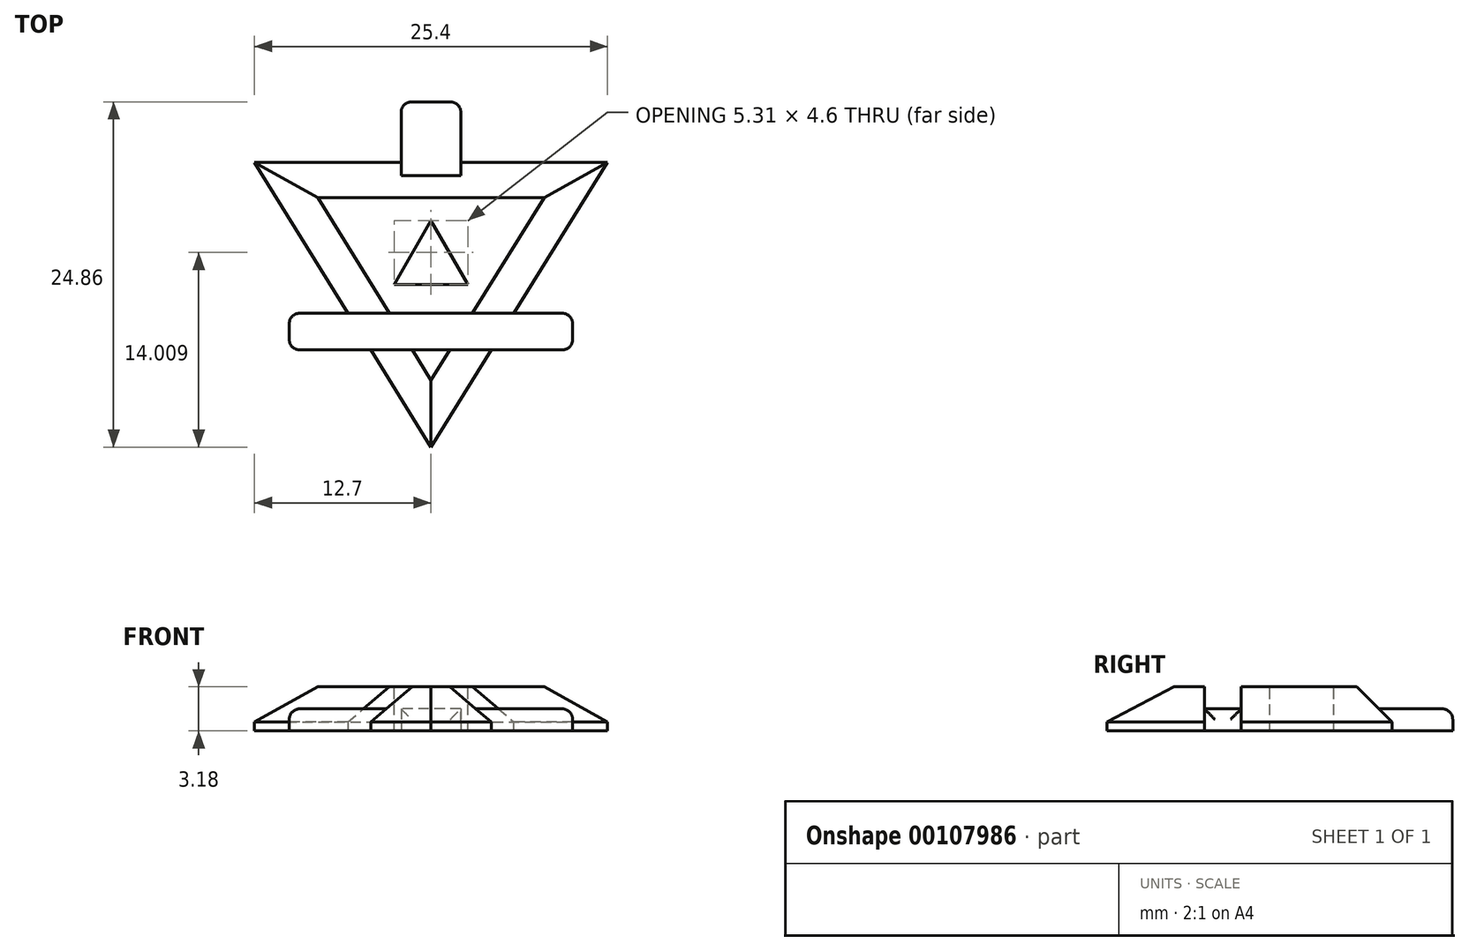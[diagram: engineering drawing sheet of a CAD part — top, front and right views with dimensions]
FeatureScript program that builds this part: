
annotation { "Feature Type Name" : "Feature", "Feature Type Description" : "" }
export const myFeature = defineFeature(function(context is Context, id is Id, definition is map)
    precondition{}
    {
        {
            var Q0;
            Q0=qCreatedBy(makeId("Top.planeOp"),FACE);
            var sketch = newSketch(context, id + "F0", { "sketchPlane" : qUnion([Q0])});
            skLineSegment(sketch, "E0.bottom", {"start": v(-12.7, 12.7) * mm, "end": v(12.7, 12.7) * mm});
            skLineSegment(sketch, "E0.top", {"start": v(-12.7, -12.7) * mm, "end": v(12.7, -12.7) * mm});
            skLineSegment(sketch, "E0.left", {"start": v(-12.7, 12.7) * mm, "end": v(-12.7, -12.7) * mm});
            skLineSegment(sketch, "E0.right", {"start": v(12.7, 12.7) * mm, "end": v(12.7, -12.7) * mm});
            skPoint(sketch, "E0.middle", {"position": v(0, 0) * mm});
            skLineSegment(sketch, "E1", {"start": v(0, -12.7) * mm, "end": v(-12.7, 7.8) * mm});
            skLineSegment(sketch, "E2", {"start": v(-12.7, 7.8) * mm, "end": v(12.7, 7.8) * mm});
            skLineSegment(sketch, "E3", {"start": v(12.7, 7.8) * mm, "end": v(0, -12.7) * mm});
            skSolve(sketch);
        }
        {
            var Q0;
            Q0=makeQuery(id+"F0.imprint","IMPRINT",FACE,{"disambiguationData":[TD([[makeQuery(id+"F0.imprint","IMPRINT",EDGE,{"derivedFrom":sQuery(id+"F0.wireOp",EDGE,"E1")}),-1.0]])]});
            extrude(context, id + "F1", {"entities" : qUnion([Q0]), "depth" : 3.17 * mm});
        }
        {
            var Q0;
            Q0=qCreatedBy(makeId("Top.planeOp"),FACE);
            var sketch = newSketch(context, id + "F2", { "sketchPlane" : qUnion([Q0])});
            skLineSegment(sketch, "E4.bottom", {"start": v(-10.2, -3.06) * mm, "end": v(10.2, -3.06) * mm});
            skLineSegment(sketch, "E4.top", {"start": v(-10.2, -5.7) * mm, "end": v(10.2, -5.7) * mm});
            skLineSegment(sketch, "E4.left", {"start": v(-10.2, -3.06) * mm, "end": v(-10.2, -5.7) * mm});
            skLineSegment(sketch, "E4.right", {"start": v(10.2, -3.06) * mm, "end": v(10.2, -5.7) * mm});
            skPoint(sketch, "E4.middle", {"position": v(0, -4.38) * mm});
            skLineSegment(sketch, "E5.bottom", {"start": v(2.15, 12.16) * mm, "end": v(-2.15, 12.16) * mm});
            skLineSegment(sketch, "E5.top", {"start": v(2.15, -1.67) * mm, "end": v(-2.15, -1.67) * mm});
            skLineSegment(sketch, "E5.left", {"start": v(2.15, 12.16) * mm, "end": v(2.15, -1.67) * mm});
            skLineSegment(sketch, "E5.right", {"start": v(-2.15, 12.16) * mm, "end": v(-2.15, -1.67) * mm});
            skPoint(sketch, "E5.middle", {"position": v(0, 5.25) * mm});
            skSolve(sketch);
        }
        {
            var Q0;
            Q0 = qSketchRegion(id + "F2", true);
            extrude(context, id + "F3", {"entities" : qUnion([Q0]), "operationType" : NewBodyOperationType.ADD, "depth" : 1.59 * mm});
        }
        {
            var Q0;
            {var subQ0=sQuery(id+"F2.wireOp",EDGE,"E4.right");var subQ1=sQuery(id+"F2.wireOp",EDGE,"E4.bottom");var subQ2=sQuery(id+"F2.wireOp",EDGE,"E4.top");Q0=makeQuery(id+"F3.boolean.opBoolean","SPLIT",FACE,{"disambiguationData":[TD([makeQuery(id+"F1.opExtrude","SWEPT_FACE",FACE,{"disambiguationData":[OSD([sQuery(id+"F0.wireOp",EDGE,"E3")])]})])],"derivedFrom":makeQuery(id+"F3.opExtrude","CAP_FACE",FACE,{"disambiguationData":[OSD([subQ1,subQ2,sQuery(id+"F2.wireOp",EDGE,"E4.left"),subQ0])],"isStart":false})});}
            var sketch = newSketch(context, id + "F4", { "sketchPlane" : qUnion([Q0])});
            skLineSegment(sketch, "E6.bottom", {"start": v(5.97, -3.06) * mm, "end": v(-8.4, -3.06) * mm});
            skLineSegment(sketch, "E6.top", {"start": v(5.97, -5.7) * mm, "end": v(-8.4, -5.7) * mm});
            skLineSegment(sketch, "E6.left", {"start": v(5.97, -3.06) * mm, "end": v(5.97, -5.7) * mm});
            skLineSegment(sketch, "E6.right", {"start": v(-8.4, -3.06) * mm, "end": v(-8.4, -5.7) * mm});
            skSolve(sketch);
        }
        {
            var Q0;
            Q0 = qSketchRegion(id + "F4", true);
            extrude(context, id + "F5", {"entities" : qUnion([Q0]), "operationType" : NewBodyOperationType.REMOVE, "depth" : 25.4 * mm});
        }
        {
            var Q0;
            {var subQ0=sQuery(id+"F0.wireOp",EDGE,"E1");var subQ1=sQuery(id+"F0.wireOp",EDGE,"E2");Q0=makeQuery(id+"F5.boolean.opBoolean","SPLIT",EDGE,{"disambiguationData":[TD([makeQuery(id+"F1.opExtrude","SWEPT_FACE",FACE,{"disambiguationData":[OSD([subQ1])]})])],"derivedFrom":makeQuery(id+"F1.opExtrude","CAP_EDGE",EDGE,{"disambiguationData":[OSD([subQ0])],"isStart":false})});}
            var Q1;
            Q1=makeQuery(id+"F1.opExtrude","CAP_EDGE",EDGE,{"disambiguationData":[OSD([sQuery(id+"F0.wireOp",EDGE,"E2")])],"isStart":false});
            var Q2;
            {var subQ0=sQuery(id+"F0.wireOp",EDGE,"E3");var subQ1=sQuery(id+"F0.wireOp",EDGE,"E2");Q2=makeQuery(id+"F5.boolean.opBoolean","SPLIT",EDGE,{"disambiguationData":[TD([makeQuery(id+"F1.opExtrude","SWEPT_FACE",FACE,{"disambiguationData":[OSD([subQ1])]})])],"derivedFrom":makeQuery(id+"F1.opExtrude","CAP_EDGE",EDGE,{"disambiguationData":[OSD([subQ0])],"isStart":false})});}
            var Q3;
            {var subQ0=sQuery(id+"F0.wireOp",EDGE,"E1");var subQ1=sQuery(id+"F0.wireOp",EDGE,"E3");Q3=makeQuery(id+"F5.boolean.opBoolean","SPLIT",EDGE,{"disambiguationData":[TD([makeQuery(id+"F1.opExtrude","SWEPT_FACE",FACE,{"disambiguationData":[OSD([subQ0])]})])],"derivedFrom":makeQuery(id+"F1.opExtrude","CAP_EDGE",EDGE,{"disambiguationData":[OSD([subQ1])],"isStart":false})});}
            var Q4;
            {var subQ0=sQuery(id+"F0.wireOp",EDGE,"E1");var subQ1=sQuery(id+"F0.wireOp",EDGE,"E3");Q4=makeQuery(id+"F5.boolean.opBoolean","SPLIT",EDGE,{"disambiguationData":[TD([makeQuery(id+"F1.opExtrude","SWEPT_FACE",FACE,{"disambiguationData":[OSD([subQ1])]})])],"derivedFrom":makeQuery(id+"F1.opExtrude","CAP_EDGE",EDGE,{"disambiguationData":[OSD([subQ0])],"isStart":false})});}
            chamfer(context, id + "F6", {"entities" : qUnion([Q0, Q1, Q2, Q3, Q4]), "width" : 2.54 * mm, "tangentPropagation" : true});
        }
        {
            var Q0;
            Q0=makeQuery(id+"F3.opExtrude","SWEPT_EDGE",EDGE,{"disambiguationData":[OSD([sQuery(id+"F2.wireOp",EDGE,"E5.bottom"),sQuery(id+"F2.wireOp",EDGE,"E5.right")])]});
            var Q1;
            Q1=makeQuery(id+"F3.opExtrude","CAP_EDGE",EDGE,{"disambiguationData":[OSD([sQuery(id+"F2.wireOp",EDGE,"E5.bottom")])],"isStart":false});
            var Q2;
            Q2=makeQuery(id+"F3.opExtrude","SWEPT_EDGE",EDGE,{"disambiguationData":[OSD([sQuery(id+"F2.wireOp",EDGE,"E5.bottom"),sQuery(id+"F2.wireOp",EDGE,"E5.left")])]});
            var Q3;
            Q3=makeQuery(id+"F3.opExtrude","CAP_EDGE",EDGE,{"disambiguationData":[OSD([sQuery(id+"F2.wireOp",EDGE,"E4.left")])],"isStart":false});
            var Q4;
            Q4=makeQuery(id+"F3.opExtrude","SWEPT_EDGE",EDGE,{"disambiguationData":[OSD([sQuery(id+"F2.wireOp",EDGE,"E4.top"),sQuery(id+"F2.wireOp",EDGE,"E4.left")])]});
            var Q5;
            Q5=makeQuery(id+"F3.opExtrude","SWEPT_EDGE",EDGE,{"disambiguationData":[OSD([sQuery(id+"F2.wireOp",EDGE,"E4.bottom"),sQuery(id+"F2.wireOp",EDGE,"E4.left")])]});
            var Q6;
            Q6=makeQuery(id+"F3.opExtrude","SWEPT_EDGE",EDGE,{"disambiguationData":[OSD([sQuery(id+"F2.wireOp",EDGE,"E4.bottom"),sQuery(id+"F2.wireOp",EDGE,"E4.right")])]});
            var Q7;
            Q7=makeQuery(id+"F3.opExtrude","SWEPT_EDGE",EDGE,{"disambiguationData":[OSD([sQuery(id+"F2.wireOp",EDGE,"E4.top"),sQuery(id+"F2.wireOp",EDGE,"E4.right")])]});
            var Q8;
            Q8=makeQuery(id+"F3.opExtrude","CAP_EDGE",EDGE,{"disambiguationData":[OSD([sQuery(id+"F2.wireOp",EDGE,"E4.right")])],"isStart":false});
            fillet(context, id + "F7", {"entities" : qUnion([Q0, Q1, Q2, Q3, Q4, Q5, Q6, Q7, Q8]), "radius" : 0.76 * mm, "tangentPropagation" : true, "allowEdgeOverflow" : false});
        }
        {
            var Q0;
            {var subQ0=sQuery(id+"F0.wireOp",EDGE,"E1");var subQ1=sQuery(id+"F0.wireOp",EDGE,"E2");var subQ2=sQuery(id+"F0.wireOp",EDGE,"E3");Q0=makeQuery(id+"F5.boolean.opBoolean","SPLIT",FACE,{"disambiguationData":[TD([makeQuery(id+"F1.opExtrude","SWEPT_FACE",FACE,{"disambiguationData":[OSD([subQ1])]})])],"derivedFrom":makeQuery(id+"F1.opExtrude","CAP_FACE",FACE,{"disambiguationData":[OSD([subQ0,subQ1,subQ2])],"isStart":false})});}
            var sketch = newSketch(context, id + "F8", { "sketchPlane" : qUnion([Q0])});
            skLineSegment(sketch, "E7", {"start": v(0, -0.99) * mm, "end": v(2.65, -0.99) * mm});
            skLineSegment(sketch, "E8", {"start": v(2.65, -0.99) * mm, "end": v(0, 3.6) * mm});
            skLineSegment(sketch, "E9", {"start": v(0, 3.6) * mm, "end": v(-2.65, -0.99) * mm});
            skLineSegment(sketch, "E10", {"start": v(-2.65, -0.99) * mm, "end": v(0, -0.99) * mm});
            skSolve(sketch);
        }
        {
            var Q0;
            Q0 = qSketchRegion(id + "F8", true);
            extrude(context, id + "F9", {"entities" : qUnion([Q0]), "operationType" : NewBodyOperationType.REMOVE, "oppositeDirection" : true, "depth" : 25.4 * mm});
        }
    });
